# Revit family: Geberit uređaj za ispiranje WC-a sa elektronskim aktiviranjem ispiranja, mrežno napajanje, dvokoličinsko ispiranje, tipka za aktiviranje Sigma80, beskontaktno_PRO_2159419
name_source: partatom
category: Furniture
units: mm (PartAtom-declared; Revit-internal decimal feet)

## family parameters
Always vertical = Yes
Cut with Voids When Loaded = No
OmniClass Number = 23.40.20.21
OmniClass Title = Toilet and Bath Specialties
Room Calculation Point = Yes
Shared = No
Work Plane-Based = No

## types (2) — shared parameters
116090_0_view = Yes
B = 24.7 cm
BIM datoteka, datum izmene = 2020.05.18
BIM datoteka, proizvođač = Geberit
BIM datoteka, verzija = GEB MG 1.2
CW Connection = Yes
Description = Geberit uređaj za ispiranje WC-a sa elektronskim aktiviranjem ispiranja, mrežno napajanje, dvokoličinsko ispiranje, tipka za aktiviranje Sigma80, beskontaktno
GEB_culture = sr-RS
GEB_generic_description = GBC
GEB_generic_manufacturer = generic
GEB_pimversion = 23.02.17
GEB_processing_type = T
GEB_reference = PRO_2159419
GEB_translations = {"ATT_10673":"EAN code basic data","ATT_10931":"B","ATT_10951":"H","ATT_380239":"T","ATT_459792":"Boja / površina","applicationPurposes":"Namene","application_range":"Oblast primene","brandName":"Robna marka","characteristics":"Svojstva","content_creator":"BIM datoteka, proizvođač","content_date_changed":"BIM datoteka, datum izmene","content_version":"BIM datoteka, verzija","key 1000":"Broj artikla","name":"Naziv","productBrand":"Robna marka proizvoda","scopeOfDelivery":"Obim isporuke","type":"Tip","fixed_material":"Osnovni materijal"}
H = 16.4 cm
HW Connection = No
IfcDescription = Geberit uređaj za ispiranje WC-a sa elektronskim aktiviranjem ispiranja, mrežno napajanje, dvokoličinsko ispiranje, tipka za aktiviranje Sigma80, beskontaktno
IfcExportAs = IfcUnitaryControlElement
IfcExportType = CONTROLPANEL
LOD300 = No
LOD400 = Yes
Manufacturer = Geberit
Model = Sigma80
Namene = Za privatne i polujavne površine
Za aktiviranje dvokoličinskog ispiranja
Za masivnu i suvu konstrukciju
Za beskontaktno aktiviranje ispiranja Sigma ugradnih vodokotlića 12 cm
Nije pogodno za upotrebu sa Geberit okvirima za ubacivanje dezinfekcijskih kocki u UP300/320 vodokotlić
Pogodno za ugradnju u prostorije za osobe sa invaliditetom
Naziv = Geberit uređaj za ispiranje WC-a sa elektronskim aktiviranjem ispiranja, mrežno napajanje, dvokoličinsko ispiranje, tipka za aktiviranje Sigma80, beskontaktno
Obim isporuke = Sigma80 tipka za aktiviranje
Montažni okvir
Nosač poluga sa servo motorom i uređajem za podizanje, predmontirani
Oblast primene = Furniture
Osnovni materijal = Geberit, Plastic, Opaque white
Robna marka = Geberit
Svojstva = Ručno pokretanje ispiranja, beskontaktno
Automatsko pokretanje ispiranja, sa mogućnošću aktiviranja
Aktiviranje ispiranja, moguće preko eksternog tastera
Tipka za aktiviranje bez mehaničkih tastera
Tasteri prepoznatljivi po svetlećim stubićima
Osvetljenje tastera aktivira se pri približavanju
Osvetljenje tastera je podesivo u pet boja
Svetlo za orijentaciju, sa mogućnošću uključivanja
Napajanje strujom preko eksterne jedinice napajanja
Transformacija mrežnog napona u nizak napon 12 V DC
Rad pod niskim naponom, bez mrežnog napona u vodokotliću
Sa utičnicom koja se ne može greškom zameniti
Infracrvena detekcija korisnika sa ignorisanjem pozadine
IC senzor, samopodešavajući
Sigurna detekcija rastojanja pomoću infracrvenih zraka
Podesivi opseg detekcije korisnika
Interval ispiranja, podesiv
Predispiranje, podesivo
Minimalno vreme zadržavanja, podesivo
Podešavanja uređaja i rukovanje pomoću mobilnog uređaja putem integrisanog Bluetooth® interfejsa
Kompatibilno sa Geberit Control aplikacijom
Bežično povezivanje sa Geberit mrežnim prolazom putem GEBUS konvertera
Bežično povezivanje sa Geberit mrežnim prolazom preko Bluetooth® veze
Kompatibilno sa Geberit Connect
Kompatibilno sa Geberit servisnim upravljačem
Aktiviranje ispiranja, može se deaktivirati
Mehanizam za podizanje, niskošumni
Električni uređaj za podizanje, sa samostalnom kalibracijom
Sa mogućnošću zaključavanja
Lako se održava i čisti
T = 1 cm
Tip = Sigma80
Vent Connection = No
Waste Connection = Yes
zero-valued in all types: Default Elevation

## per-type parameters (varying)
| type | Boja / površina | Broj artikla | EAN code basic data |
| 116.090.SG.6 Geberit uređaj za ispiranje WC-a sa elektronskim aktiviranjem ispiranja, mrežno napajanje, dvokoličinsko ispiranje, tipka za aktiviranje Sigma80, beskontaktno | crna / staklo sa reflektujućim premazom | 116.090.SG.6 | 4025410532114 |
| 116.090.SM.6 Geberit uređaj za ispiranje WC-a sa elektronskim aktiviranjem ispiranja, mrežno napajanje, dvokoličinsko ispiranje, tipka za aktiviranje Sigma80, beskontaktno | staklo sa reflektujućim premazom | 116.090.SM.6 | 4025410531841 |

## geometry (parser evidence)
native form markers: Blend x8, Sweep x11
no freeform markers — native parametric forms only
